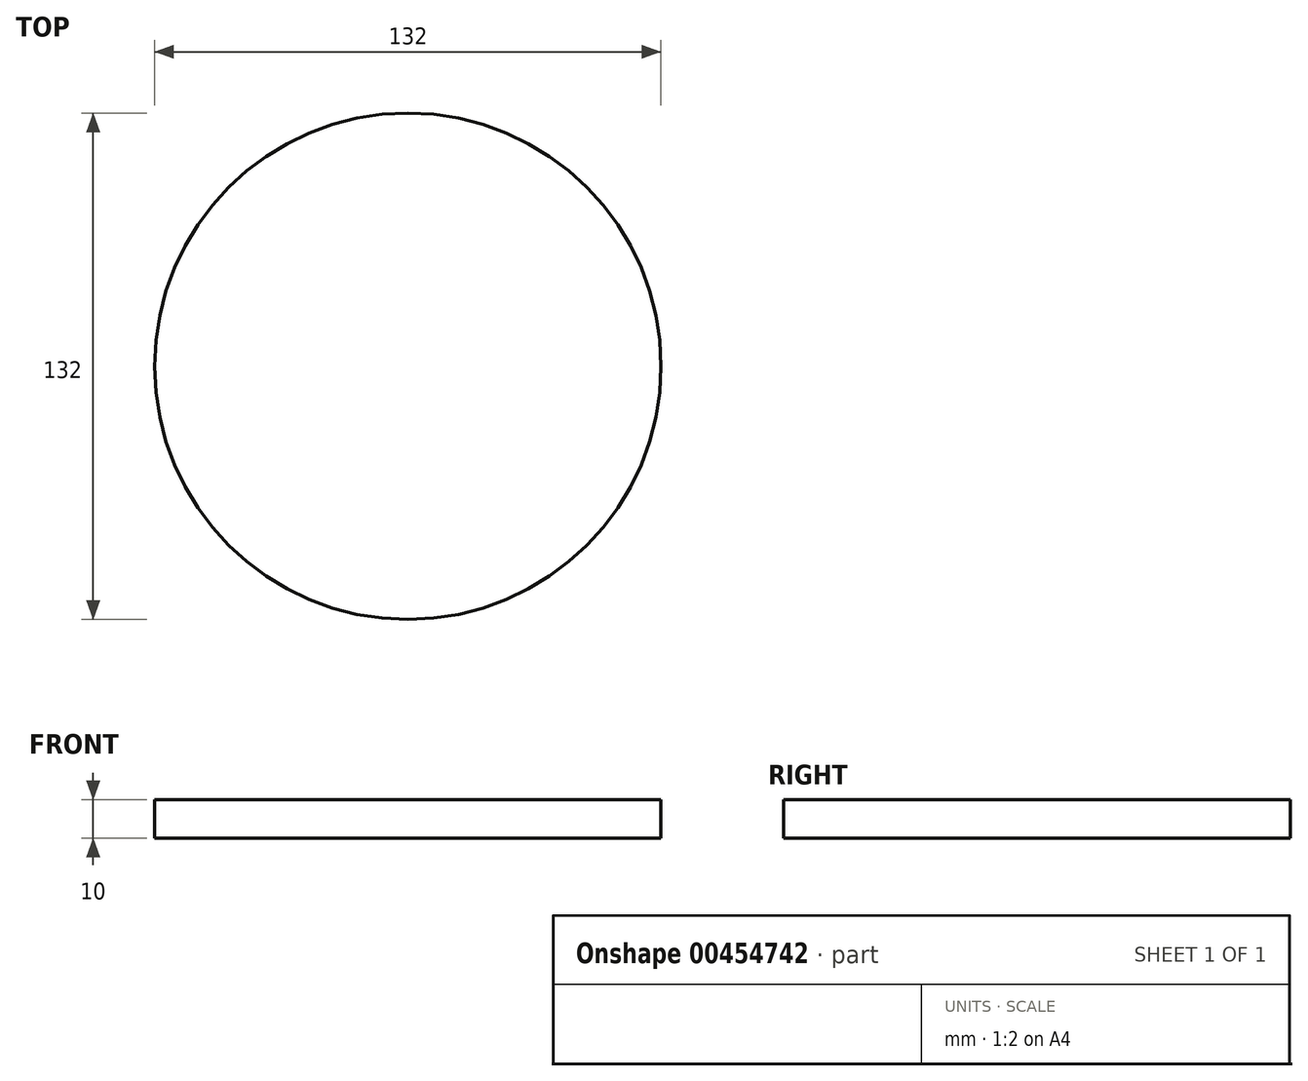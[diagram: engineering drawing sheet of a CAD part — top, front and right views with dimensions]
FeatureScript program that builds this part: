
annotation { "Feature Type Name" : "Feature", "Feature Type Description" : "" }
export const myFeature = defineFeature(function(context is Context, id is Id, definition is map)
    precondition{}
    {
        {
            var Q0;
            Q0=qCreatedBy(makeId("Top.planeOp"),FACE);
            var sketch = newSketch(context, id + "F0", { "sketchPlane" : qUnion([Q0])});
            skCircle(sketch, "E0", {"center": v(0, 0) * mm, "radius": 66 * mm});
            skSolve(sketch);
        }
        {
            var Q0;
            Q0 = qSketchRegion(id + "F0", true);
            extrude(context, id + "F1", {"entities" : qUnion([Q0]), "depth" : 10 * mm});
        }
    });
